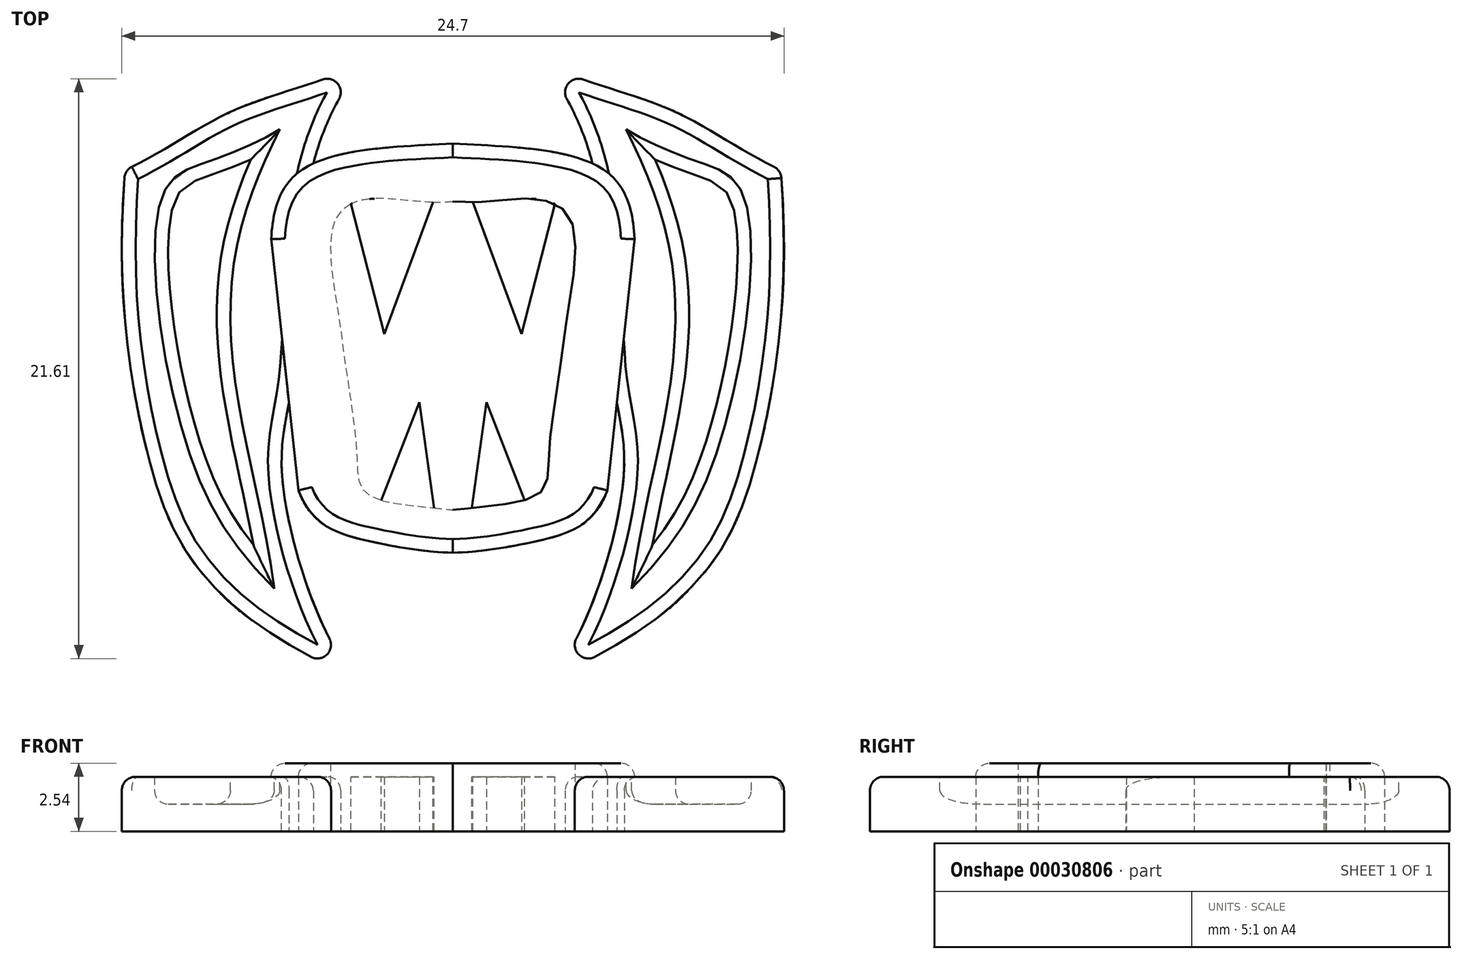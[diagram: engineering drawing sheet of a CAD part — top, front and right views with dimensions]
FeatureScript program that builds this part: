
annotation { "Feature Type Name" : "Feature", "Feature Type Description" : "" }
export const myFeature = defineFeature(function(context is Context, id is Id, definition is map)
    precondition{}
    {
        {
            var Q0;
            Q0=qCreatedBy(makeId("Top.planeOp"),FACE);
            var sketch = newSketch(context, id + "F0", { "sketchPlane" : qUnion([Q0])});
            skLineSegment(sketch, "E0.rect.bottom", {"start": v(12.7, 12.7) * mm, "end": v(-12.7, 12.7) * mm});
            skLineSegment(sketch, "E0.rect.top", {"start": v(12.7, -12.7) * mm, "end": v(-12.7, -12.7) * mm});
            skLineSegment(sketch, "E0.rect.left", {"start": v(12.7, 12.7) * mm, "end": v(12.7, -12.7) * mm});
            skLineSegment(sketch, "E0.rect.right", {"start": v(-12.7, 12.7) * mm, "end": v(-12.7, -12.7) * mm});
            skPoint(sketch, "E0.rect.middle", {"position": v(0, 0) * mm});
            skLineSegment(sketch, "E1", {"start": v(0, 12.7) * mm, "end": v(0, -12.7) * mm});
            skFitSpline(sketch, "E2", {"points": [v(0, 8.95) * mm, v(-5.33, 8.16) * mm, v(-6.78, 5.4) * mm], "startDerivative": vector(-10.3, -0.5) * mm, "endDerivative": vector(-0.5, -10.08) * mm});
            skLineSegment(sketch, "E3", {"start": v(-6.78, 5.4) * mm, "end": v(-5.76, -3.97) * mm});
            skFitSpline(sketch, "E4", {"points": [v(-5.76, -3.97) * mm, v(-3.15, -5.86) * mm, v(0, -6.3) * mm], "startDerivative": vector(3.04, -8.25) * mm, "endDerivative": vector(6.6, -0.16) * mm});
            skFitSpline(sketch, "E5.MirrorCS", {"points": [v(0, 8.95) * mm, v(5.33, 8.16) * mm, v(6.78, 5.4) * mm], "startDerivative": vector(10.3, -0.5) * mm, "endDerivative": vector(0.5, -10.08) * mm});
            skLineSegment(sketch, "E6.MirrorCS", {"start": v(6.78, 5.4) * mm, "end": v(5.76, -3.97) * mm});
            skFitSpline(sketch, "E7.MirrorCS", {"points": [v(5.76, -3.97) * mm, v(3.15, -5.86) * mm, v(0, -6.3) * mm], "startDerivative": vector(-3.04, -8.25) * mm, "endDerivative": vector(-6.6, -0.16) * mm});
            skSolve(sketch);
        }
        {
            var Q0;
            {var subQ1=sQuery(id+"F0.wireOp",EDGE,"E2");Q0=makeQuery(id+"F0.imprint","IMPRINT",FACE,{"disambiguationData":[TD([[makeQuery(id+"F0.imprint","IMPRINT",EDGE,{"derivedFrom":subQ1}),1.0]])]});}
            var Q1;
            {var subQ1=sQuery(id+"F0.wireOp",EDGE,"E5.MirrorCS");Q1=makeQuery(id+"F0.imprint","IMPRINT",FACE,{"disambiguationData":[TD([[makeQuery(id+"F0.imprint","IMPRINT",EDGE,{"derivedFrom":subQ1}),-1.0]])]});}
            extrude(context, id + "F1", {"entities" : qUnion([Q0, Q1]), "depth" : 2.54 * mm});
        }
        {
            var Q0;
            Q0=qCreatedBy(makeId("Top.planeOp"),FACE);
            var sketch = newSketch(context, id + "F2", { "sketchPlane" : qUnion([Q0])});
            skLineSegment(sketch, "E8", {"start": v(0, 0) * mm, "end": v(0, 10.15) * mm});
            skFitSpline(sketch, "E9", {"points": [v(-3.21, 12.1) * mm, v(-7.95, 10.29) * mm, v(-12.23, 7.96) * mm], "startDerivative": vector(-7.35, -4.67) * mm, "endDerivative": vector(-10.73, -5.16) * mm});
            skFitSpline(sketch, "E10", {"points": [v(-12.23, 7.96) * mm, v(-12.23, 2.4) * mm, v(-10.67, -4.86) * mm, v(-8.94, -7.53) * mm, v(-3.58, -11.08) * mm], "startDerivative": vector(-1.33, -19.36) * mm, "endDerivative": vector(37.7, -19.1) * mm});
            skFitSpline(sketch, "E11", {"points": [v(-3.58, -11.08) * mm, v(-6.37, -3.4) * mm, v(-6, 0) * mm, v(-5.57, 6.27) * mm, v(-3.21, 12.1) * mm], "startDerivative": vector(-15.47, 18.26) * mm, "endDerivative": vector(17.29, 20.3) * mm});
            skFitSpline(sketch, "E12.MirrorCS", {"points": [v(3.58, -11.08) * mm, v(6.37, -3.4) * mm, v(6, 0) * mm, v(5.57, 6.27) * mm, v(3.21, 12.1) * mm], "startDerivative": vector(15.47, 18.26) * mm, "endDerivative": vector(-17.29, 20.3) * mm});
            skFitSpline(sketch, "E13.MirrorCS", {"points": [v(3.21, 12.1) * mm, v(7.95, 10.29) * mm, v(12.23, 7.96) * mm], "startDerivative": vector(7.35, -4.67) * mm, "endDerivative": vector(10.73, -5.16) * mm});
            skFitSpline(sketch, "E14.MirrorCS", {"points": [v(12.23, 7.96) * mm, v(12.23, 2.4) * mm, v(10.67, -4.86) * mm, v(8.94, -7.53) * mm, v(3.58, -11.08) * mm], "startDerivative": vector(1.33, -19.36) * mm, "endDerivative": vector(-37.7, -19.1) * mm});
            skSolve(sketch);
        }
        {
            var Q0;
            Q0 = qSketchRegion(id + "F2", true);
            extrude(context, id + "F3", {"entities" : qUnion([Q0]), "operationType" : NewBodyOperationType.ADD, "depth" : 2.03 * mm});
        }
        {
            var Q0;
            Q0=makeQuery(id+"F3.opExtrude","SWEPT_EDGE",EDGE,{"disambiguationData":[OSD([sQuery(id+"F2.wireOp",EDGE,"E10"),sQuery(id+"F2.wireOp",EDGE,"E11")])]});
            var Q1;
            Q1=makeQuery(id+"F3.opExtrude","SWEPT_EDGE",EDGE,{"disambiguationData":[OSD([sQuery(id+"F2.wireOp",EDGE,"E12.MirrorCS"),sQuery(id+"F2.wireOp",EDGE,"E14.MirrorCS")])]});
            var Q2;
            Q2=makeQuery(id+"F3.opExtrude","SWEPT_EDGE",EDGE,{"disambiguationData":[OSD([sQuery(id+"F2.wireOp",EDGE,"E9"),sQuery(id+"F2.wireOp",EDGE,"E10")])]});
            var Q3;
            Q3=makeQuery(id+"F3.opExtrude","SWEPT_EDGE",EDGE,{"disambiguationData":[OSD([sQuery(id+"F2.wireOp",EDGE,"E12.MirrorCS"),sQuery(id+"F2.wireOp",EDGE,"E13.MirrorCS")])]});
            var Q4;
            Q4=makeQuery(id+"F3.opExtrude","SWEPT_EDGE",EDGE,{"disambiguationData":[OSD([sQuery(id+"F2.wireOp",EDGE,"E9"),sQuery(id+"F2.wireOp",EDGE,"E11")])]});
            var Q5;
            Q5=makeQuery(id+"F3.opExtrude","SWEPT_EDGE",EDGE,{"disambiguationData":[OSD([sQuery(id+"F2.wireOp",EDGE,"E13.MirrorCS"),sQuery(id+"F2.wireOp",EDGE,"E14.MirrorCS")])]});
            fillet(context, id + "F4", {"entities" : qUnion([Q0, Q1, Q2, Q3, Q4, Q5]), "radius" : 0.5 * mm, "tangentPropagation" : true, "allowEdgeOverflow" : false});
        }
        {
            var Q0;
            Q0=makeQuery(id+"F1.opExtrude","CAP_FACE",FACE,{"disambiguationData":[OSD([sQuery(id+"F0.wireOp",EDGE,"E2"),sQuery(id+"F0.wireOp",EDGE,"E3"),sQuery(id+"F0.wireOp",EDGE,"E4"),sQuery(id+"F0.wireOp",EDGE,"E5.MirrorCS"),sQuery(id+"F0.wireOp",EDGE,"E6.MirrorCS"),sQuery(id+"F0.wireOp",EDGE,"E7.MirrorCS")])],"isStart":false});
            var sketch = newSketch(context, id + "F5", { "sketchPlane" : qUnion([Q0])});
            skFitSpline(sketch, "E15", {"points": [v(0, 6.8) * mm, v(-2.97, 6.9) * mm, v(-4.41, 6.08) * mm, v(-4.3, 2.85) * mm, v(-4, 0.64) * mm, v(-3.59, -2.54) * mm, v(-3.28, -4.03) * mm, v(-1.43, -4.55) * mm, v(0, -4.7) * mm], "startDerivative": vector(-21.68, -2.43) * mm, "endDerivative": vector(12.9, -1.37) * mm});
            skLineSegment(sketch, "E16", {"start": v(0, 6.8) * mm, "end": v(0, 0) * mm});
            skFitSpline(sketch, "E17.MirrorCS", {"points": [v(0, 6.8) * mm, v(2.97, 6.9) * mm, v(4.41, 6.08) * mm, v(4.3, 2.85) * mm, v(4, 0.64) * mm, v(3.59, -2.54) * mm, v(3.28, -4.03) * mm, v(1.43, -4.55) * mm, v(0, -4.7) * mm], "startDerivative": vector(21.68, -2.43) * mm, "endDerivative": vector(-12.9, -1.37) * mm});
            skSolve(sketch);
        }
        {
            var Q0;
            Q0 = qSketchRegion(id + "F5", true);
            extrude(context, id + "F6", {"entities" : qUnion([Q0]), "operationType" : NewBodyOperationType.REMOVE, "oppositeDirection" : true, "depth" : 25.4 * mm});
        }
        {
            var Q0;
            Q0=qCreatedBy(makeId("Top.planeOp"),FACE);
            var sketch = newSketch(context, id + "F7", { "sketchPlane" : qUnion([Q0])});
            skLineSegment(sketch, "E18", {"start": v(-3.95, 7.25) * mm, "end": v(-2.56, 1.85) * mm});
            skLineSegment(sketch, "E19", {"start": v(-2.56, 1.85) * mm, "end": v(-0.53, 7.34) * mm});
            skLineSegment(sketch, "E20", {"start": v(-0.53, 7.34) * mm, "end": v(-3.95, 7.25) * mm});
            skLineSegment(sketch, "E21", {"start": v(-2.93, -5) * mm, "end": v(-1.25, -0.68) * mm});
            skLineSegment(sketch, "E22", {"start": v(-1.25, -0.68) * mm, "end": v(-0.6, -5.37) * mm});
            skLineSegment(sketch, "E23", {"start": v(-0.6, -5.37) * mm, "end": v(-2.93, -5) * mm});
            skLineSegment(sketch, "E24", {"start": v(0, 0) * mm, "end": v(0, 11.4) * mm});
            skLineSegment(sketch, "E25.MirrorCS", {"start": v(2.56, 1.85) * mm, "end": v(0.53, 7.34) * mm});
            skLineSegment(sketch, "E26.MirrorCS", {"start": v(3.95, 7.25) * mm, "end": v(2.56, 1.85) * mm});
            skLineSegment(sketch, "E27.MirrorCS", {"start": v(0.53, 7.34) * mm, "end": v(3.95, 7.25) * mm});
            skLineSegment(sketch, "E28.MirrorCS", {"start": v(1.25, -0.68) * mm, "end": v(0.6, -5.37) * mm});
            skLineSegment(sketch, "E29.MirrorCS", {"start": v(2.93, -5) * mm, "end": v(1.25, -0.68) * mm});
            skLineSegment(sketch, "E30.MirrorCS", {"start": v(0.6, -5.37) * mm, "end": v(2.93, -5) * mm});
            skSolve(sketch);
        }
        {
            var Q0;
            Q0 = qSketchRegion(id + "F7", true);
            extrude(context, id + "F8", {"entities" : qUnion([Q0]), "operationType" : NewBodyOperationType.ADD, "depth" : 2.03 * mm});
        }
        {
            var Q0;
            Q0=makeQuery(id+"F3.opExtrude","CAP_FACE",FACE,{"disambiguationData":[OSD([sQuery(id+"F2.wireOp",EDGE,"E9"),sQuery(id+"F2.wireOp",EDGE,"E10"),sQuery(id+"F2.wireOp",EDGE,"E11")])],"isStart":false});
            var sketch = newSketch(context, id + "F9", { "sketchPlane" : qUnion([Q0])});
            skFitSpline(sketch, "E31", {"points": [v(-6.46, 9.48) * mm, v(-9.08, 8.3) * mm, v(-10.81, 7.08) * mm, v(-10.12, -1.65) * mm, v(-6.66, -7.63) * mm], "startDerivative": vector(-11.16, -6.87) * mm, "endDerivative": vector(17.66, -17.66) * mm});
            skFitSpline(sketch, "E32", {"points": [v(-6.46, 9.48) * mm, v(-8, 5.4) * mm, v(-8.1, 0) * mm, v(-6.66, -7.63) * mm], "startDerivative": vector(-6.06, -12.41) * mm, "endDerivative": vector(3.08, -22.2) * mm});
            skLineSegment(sketch, "E33", {"start": v(0, 0) * mm, "end": v(0, 17.4) * mm});
            skFitSpline(sketch, "E34.MirrorCS", {"points": [v(6.46, 9.48) * mm, v(9.08, 8.3) * mm, v(10.81, 7.08) * mm, v(10.12, -1.65) * mm, v(6.66, -7.63) * mm], "startDerivative": vector(11.16, -6.87) * mm, "endDerivative": vector(-17.66, -17.66) * mm});
            skFitSpline(sketch, "E35.MirrorCS", {"points": [v(6.46, 9.48) * mm, v(8, 5.4) * mm, v(8.1, 0) * mm, v(6.66, -7.63) * mm], "startDerivative": vector(6.06, -12.41) * mm, "endDerivative": vector(-3.08, -22.2) * mm});
            skSolve(sketch);
        }
        {
            var Q0;
            Q0 = qSketchRegion(id + "F9", true);
            extrude(context, id + "F10", {"entities" : qUnion([Q0]), "operationType" : NewBodyOperationType.REMOVE, "oppositeDirection" : true, "depth" : 1.02 * mm});
        }
        {
            var Q0;
            Q0=makeQuery(id+"F1.opExtrude","CAP_EDGE",EDGE,{"disambiguationData":[OSD([sQuery(id+"F0.wireOp",EDGE,"E2")])],"isStart":false});
            var Q1;
            Q1=makeQuery(id+"F1.opExtrude","CAP_EDGE",EDGE,{"disambiguationData":[OSD([sQuery(id+"F0.wireOp",EDGE,"E5.MirrorCS")])],"isStart":false});
            var Q2;
            Q2=makeQuery(id+"F1.opExtrude","CAP_EDGE",EDGE,{"disambiguationData":[OSD([sQuery(id+"F0.wireOp",EDGE,"E6.MirrorCS")])],"isStart":false});
            var Q3;
            Q3=makeQuery(id+"F1.opExtrude","CAP_EDGE",EDGE,{"disambiguationData":[OSD([sQuery(id+"F0.wireOp",EDGE,"E7.MirrorCS")])],"isStart":false});
            var Q4;
            Q4=makeQuery(id+"F1.opExtrude","CAP_EDGE",EDGE,{"disambiguationData":[OSD([sQuery(id+"F0.wireOp",EDGE,"E4")])],"isStart":false});
            var Q5;
            Q5=makeQuery(id+"F1.opExtrude","CAP_EDGE",EDGE,{"disambiguationData":[OSD([sQuery(id+"F0.wireOp",EDGE,"E3")])],"isStart":false});
            var Q6;
            Q6=makeQuery(id+"F10.boolean.opBoolean","COPY",FACE,{"derivedFrom":makeQuery(id+"F10.opExtrude","CAP_FACE",FACE,{"disambiguationData":[OSD([sQuery(id+"F9.wireOp",EDGE,"E31"),sQuery(id+"F9.wireOp",EDGE,"E32")])],"isStart":false})});
            var Q7;
            Q7=makeQuery(id+"F10.boolean.opBoolean","COPY",FACE,{"derivedFrom":makeQuery(id+"F10.opExtrude","CAP_FACE",FACE,{"disambiguationData":[OSD([sQuery(id+"F9.wireOp",EDGE,"E34.MirrorCS"),sQuery(id+"F9.wireOp",EDGE,"E35.MirrorCS")])],"isStart":false})});
            var Q8;
            Q8=makeQuery(id+"F3.opExtrude","CAP_EDGE",EDGE,{"disambiguationData":[OSD([sQuery(id+"F2.wireOp",EDGE,"E14.MirrorCS")])],"isStart":false});
            var Q9;
            Q9=makeQuery(id+"F3.opExtrude","CAP_EDGE",EDGE,{"disambiguationData":[OSD([sQuery(id+"F2.wireOp",EDGE,"E9")])],"isStart":false});
            fillet(context, id + "F11", {"entities" : qUnion([Q0, Q1, Q2, Q3, Q4, Q5, Q6, Q7, Q8, Q9]), "radius" : 0.5 * mm, "tangentPropagation" : true, "allowEdgeOverflow" : false});
        }
    });
